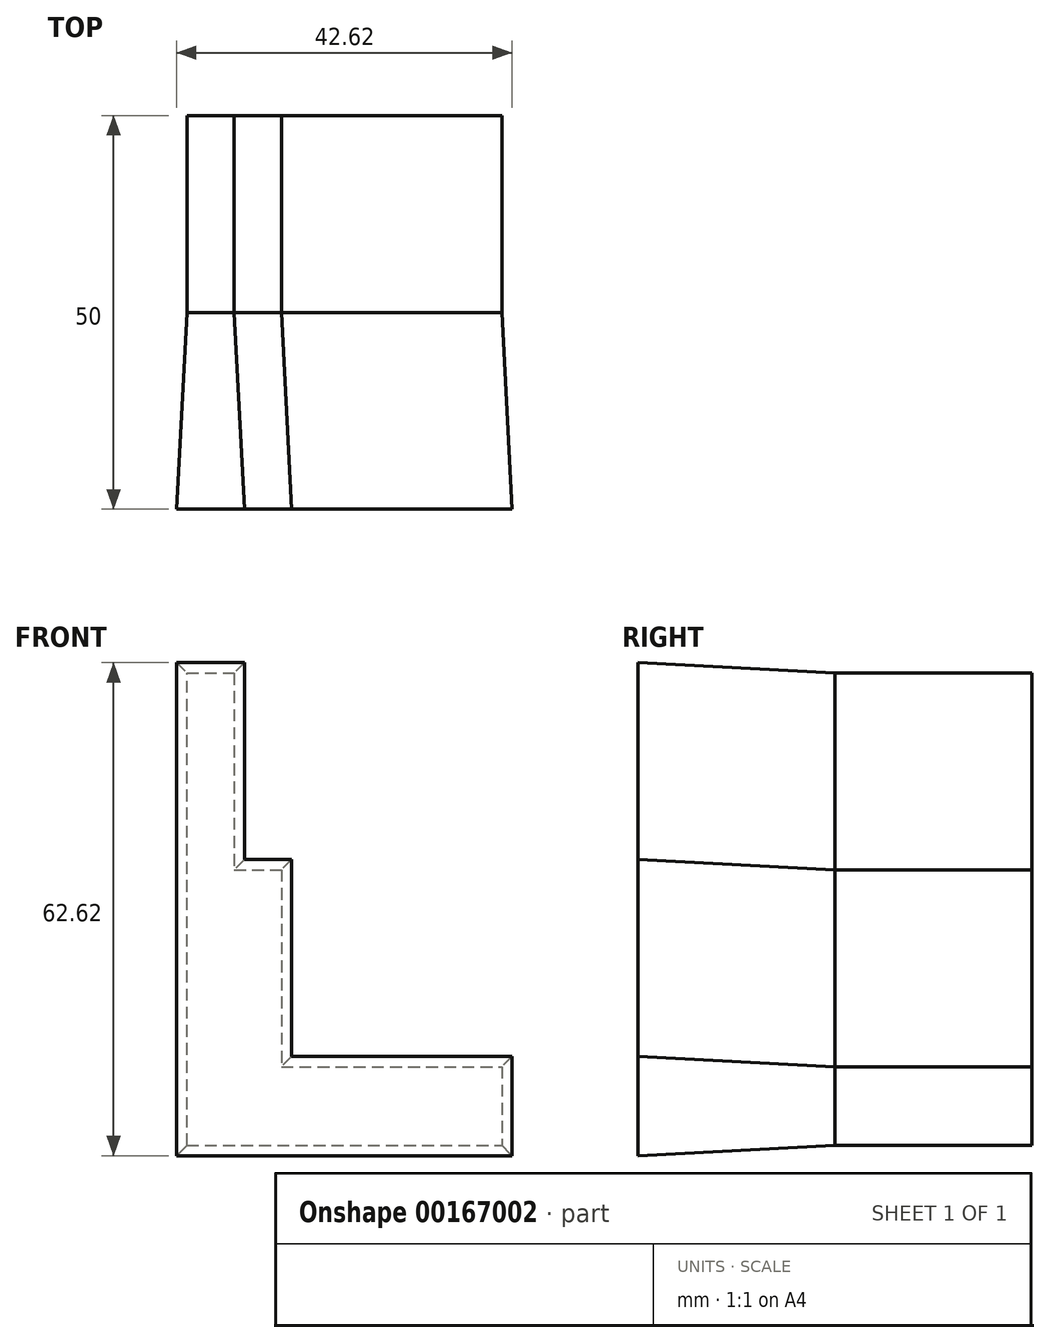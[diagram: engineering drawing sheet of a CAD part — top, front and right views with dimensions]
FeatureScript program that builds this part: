
annotation { "Feature Type Name" : "Feature", "Feature Type Description" : "" }
export const myFeature = defineFeature(function(context is Context, id is Id, definition is map)
    precondition{}
    {
        {
            var Q0;
            Q0=qCreatedBy(makeId("Front.planeOp"),FACE);
            var sketch = newSketch(context, id + "F0", { "sketchPlane" : qUnion([Q0])});
            skPoint(sketch, "E0.first.point", {"position": v(0, 0) * mm});
            skLineSegment(sketch, "E1", {"start": v(0, 0) * mm, "end": v(40, 0) * mm});
            skLineSegment(sketch, "E2", {"start": v(40, 0) * mm, "end": v(0, 0) * mm});
            skLineSegment(sketch, "E3", {"start": v(0, 0) * mm, "end": v(0, 60) * mm});
            skLineSegment(sketch, "E4", {"start": v(0, 60) * mm, "end": v(6, 60) * mm});
            skLineSegment(sketch, "E5", {"start": v(6, 60) * mm, "end": v(6, 35) * mm});
            skLineSegment(sketch, "E6", {"start": v(6, 35) * mm, "end": v(12, 35) * mm});
            skLineSegment(sketch, "E7", {"start": v(12, 35) * mm, "end": v(12, 10) * mm});
            skLineSegment(sketch, "E8", {"start": v(12, 10) * mm, "end": v(40, 10) * mm});
            skLineSegment(sketch, "E9", {"start": v(40, 10) * mm, "end": v(40, 0) * mm});
            skSolve(sketch);
        }
        {
            var Q0;
            Q0 = qSketchRegion(id + "F0", true);
            extrude(context, id + "F1", {"entities" : qUnion([Q0]), "depth" : 25 * mm, "hasDraft" : true, "draftAngle" : 3 * degree, "hasSecondDirection" : true, "secondDirectionOppositeDirection" : true, "secondDirectionDepth" : 25 * mm});
        }
    });
